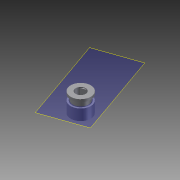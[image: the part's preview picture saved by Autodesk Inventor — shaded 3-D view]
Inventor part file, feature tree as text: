
AUTODESK INVENTOR PART (.ipt)
format: ipt  version: 2012 (Build 160160000, 160)  size: 744,448 bytes
history: native  units: mm
features: extrude x10, sketch x10, other x3, plane x3, projected_geometry x1, reference x1
ambient origin geometry x8: Origin, YZ Plane, XZ Plane, XY Plane, X Axis, Y Axis, Z Axis, Center Point
bodies: Solid1 (feature_tree)
feature tree (28):
  other  "Spur Gear2"
  extrude  "Extrusion1"  Depth=10.0mm TaperAngle=0.0deg
  extrude  "Extrusion2"  Depth=3.570646mm
  extrude  "Extrusion3"  Depth=0.3mm
  plane  "Work Plane1"
  extrude  "Extrusion4"  Depth=2.0mm
  extrude  "Extrusion5"  Depth=1.0mm
  extrude  "Extrusion6"  Depth=0.3mm TaperAngle=0.0deg
  sketch  "Sketch8"  dims[d18=0.5mm d19=0.0mm d20=10.0mm d21=0.0mm]
  plane  "Work Plane2"
  extrude  "Extrusion7"  Depth=10.0mm TaperAngle=0.0deg
  extrude  "Extrusion8"  Depth=0.3mm TaperAngle=0.0deg
  sketch  "Sketch10"  dims[d26=22.5mm d27=10.0mm d28=0.0mm]
  plane  "Work Plane3"
  extrude  "Extrusion9"  Depth=10.0mm TaperAngle=0.0deg
  extrude  "Extrusion10"  [1 undecoded]
  other  "Solid1::Spur Gear2"
  other  "TaggingFeature1"
  sketch  "Sketch2"  dims[d0=10.0mm d1=10.0mm d2=0.0mm]
  projected_geometry  "Projected Loop1"
  sketch  "Sketch3"  dims[d3=6.0mm d4=3.570646mm]
  sketch  "Sketch4"  dims[d6=0.3mm d7=0.3mm]
  sketch  "Sketch5"  dims[d8=10.0mm d9=0.0mm d10=2.0mm]
  reference  "Reference1"
  sketch  "Sketch6"  dims[d11=8.0mm d12=0.0mm d13=1.0mm]
  sketch  "Sketch7"  dims[d14=3.0mm d15=0.0mm d16=0.3mm d17=0.0mm]
  sketch  "Sketch9"  dims[d22=0.3mm d23=0.0mm d24=0.3mm d25=0.0mm]
  sketch  "Sketch11"
note: 1 required parameter value undecoded (feature->parameter linkage not recoverable at this tier; creation-order binding heuristic only, values carry confidence <= 0.55)
